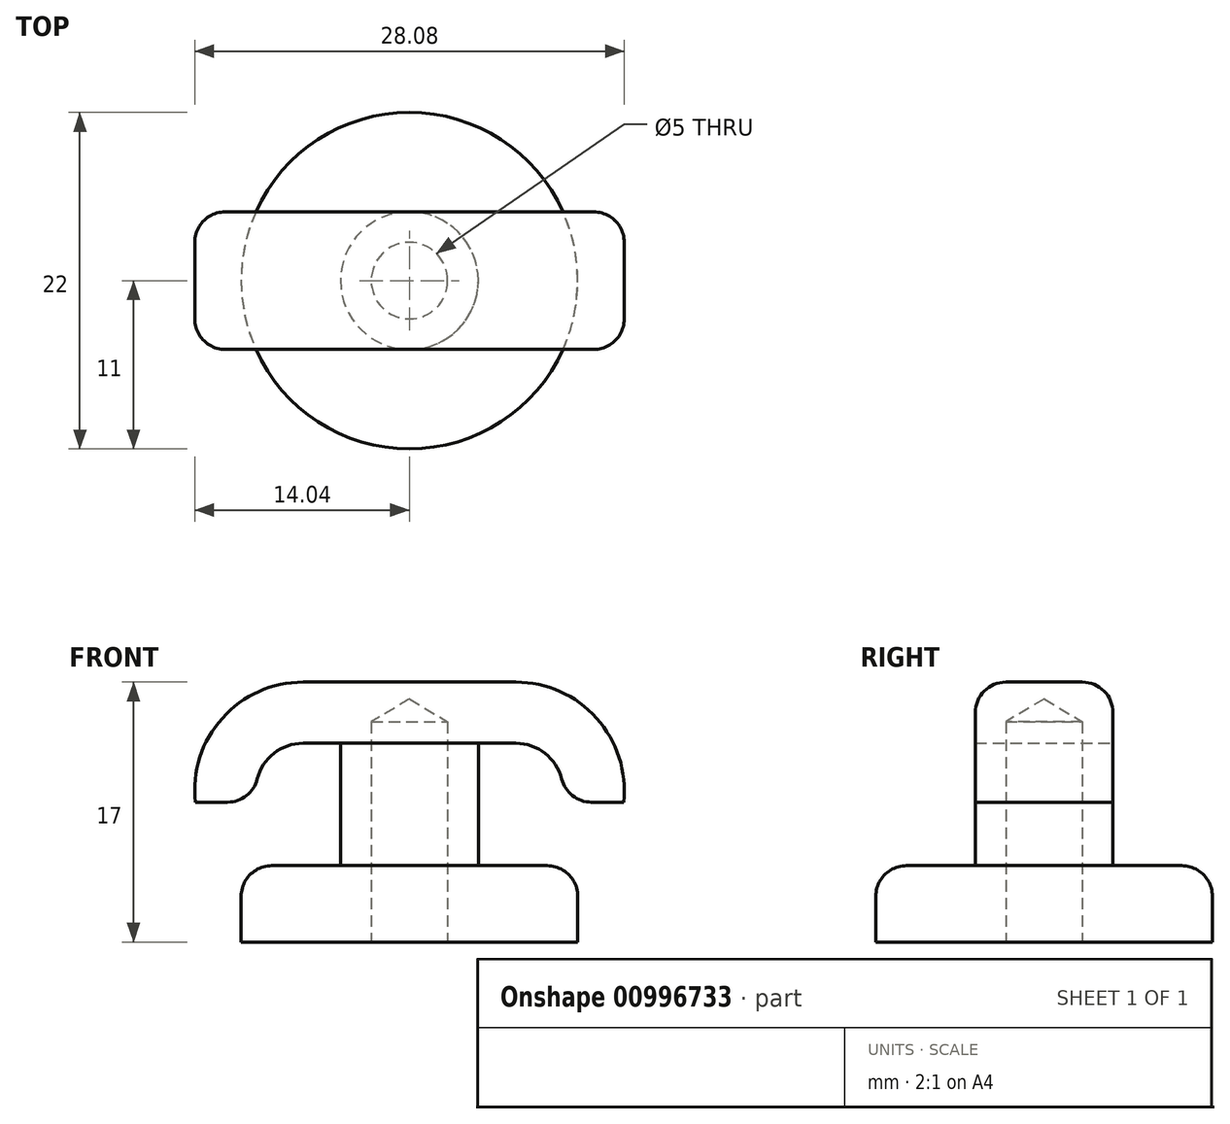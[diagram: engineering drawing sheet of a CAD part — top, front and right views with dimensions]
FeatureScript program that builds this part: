
annotation { "Feature Type Name" : "Feature", "Feature Type Description" : "" }
export const myFeature = defineFeature(function(context is Context, id is Id, definition is map)
    precondition{}
    {
        {
            var Q0;
            Q0=qCreatedBy(makeId("Top.planeOp"),FACE);
            var sketch = newSketch(context, id + "F0", { "sketchPlane" : qUnion([Q0])});
            skCircle(sketch, "E0", {"center": v(0, 0) * mm, "radius": 11 * mm});
            skSolve(sketch);
        }
        {
            var Q0;
            Q0 = qSketchRegion(id + "F0", true);
            extrude(context, id + "F1", {"entities" : qUnion([Q0]), "depth" : 5 * mm, "offsetDistance" : 25 * mm});
        }
        {
            var Q0;
            Q0=makeQuery(id+"F1.opExtrude","CAP_FACE",FACE,{"disambiguationData":[OSD([sQuery(id+"F0.wireOp",EDGE,"E0")])],"isStart":false});
            var sketch = newSketch(context, id + "F2", { "sketchPlane" : qUnion([Q0])});
            skCircle(sketch, "E1", {"center": v(0, 0) * mm, "radius": 4.5 * mm});
            skSolve(sketch);
        }
        {
            var Q0;
            Q0 = qSketchRegion(id + "F2", true);
            extrude(context, id + "F3", {"entities" : qUnion([Q0]), "operationType" : NewBodyOperationType.ADD, "depth" : 12 * mm, "offsetDistance" : 25 * mm});
        }
        {
            var Q0;
            Q0=qCreatedBy(makeId("Front.planeOp"),FACE);
            var sketch = newSketch(context, id + "F4", { "sketchPlane" : qUnion([Q0])});
            skLineSegment(sketch, "E2", {"start": v(0, 13) * mm, "end": v(6.96, 13) * mm});
            skArc(sketch, "E3", {"start": v(9.94, 9.15) * mm, "mid": v(9.4, 11.8) * mm, "end": v(6.96, 13) * mm});
            skLineSegment(sketch, "E4.0", {"start": v(0, 17) * mm, "end": v(6.96, 17) * mm});
            skArc(sketch, "E4.1", {"start": v(14, 9.15) * mm, "mid": v(12.23, 14.65) * mm, "end": v(6.96, 17) * mm});
            skLineSegment(sketch, "E5", {"start": v(9.94, 9.15) * mm, "end": v(14, 9.15) * mm});
            skArc(sketch, "E6.MirrorCS", {"start": v(-9.94, 9.15) * mm, "mid": v(-9.4, 11.8) * mm, "end": v(-6.96, 13) * mm});
            skArc(sketch, "E7.MirrorCS", {"start": v(-14, 9.15) * mm, "mid": v(-12.23, 14.65) * mm, "end": v(-6.96, 17) * mm});
            skLineSegment(sketch, "E8.MirrorCS", {"start": v(0, 13) * mm, "end": v(-6.96, 13) * mm});
            skLineSegment(sketch, "E9.MirrorCS", {"start": v(-9.94, 9.15) * mm, "end": v(-14, 9.15) * mm});
            skLineSegment(sketch, "E10.MirrorCS", {"start": v(0, 17) * mm, "end": v(-6.96, 17) * mm});
            skSolve(sketch);
        }
        {
            var Q0;
            Q0 = qSketchRegion(id + "F4", true);
            extrude(context, id + "F5", {"entities" : qUnion([Q0]), "operationType" : NewBodyOperationType.ADD, "endBound" : BoundingType.SYMMETRIC, "depth" : 9 * mm, "offsetDistance" : 25 * mm});
        }
        {
            var Q0;
            Q0=makeQuery(id+"F1.opExtrude","CAP_EDGE",EDGE,{"disambiguationData":[OSD([sQuery(id+"F0.wireOp",EDGE,"E0")])],"isStart":false});
            var Q1;
            Q1=makeQuery(id+"F5.opExtrude","CAP_EDGE",EDGE,{"disambiguationData":[OSD([sQuery(id+"F4.wireOp",EDGE,"E4.0"),sQuery(id+"F4.wireOp",EDGE,"E10.MirrorCS")])],"isStart":false});
            var Q2;
            Q2=makeQuery(id+"F5.opExtrude","CAP_EDGE",EDGE,{"disambiguationData":[OSD([sQuery(id+"F4.wireOp",EDGE,"E4.0"),sQuery(id+"F4.wireOp",EDGE,"E10.MirrorCS")])],"isStart":true});
            var Q3;
            Q3=makeQuery(id+"F5.opExtrude","SWEPT_EDGE",EDGE,{"disambiguationData":[OSD([sQuery(id+"F4.wireOp",EDGE,"E6.MirrorCS"),sQuery(id+"F4.wireOp",EDGE,"E9.MirrorCS")])]});
            var Q4;
            Q4=makeQuery(id+"F5.opExtrude","SWEPT_EDGE",EDGE,{"disambiguationData":[OSD([sQuery(id+"F4.wireOp",EDGE,"E3"),sQuery(id+"F4.wireOp",EDGE,"E5")])]});
            fillet(context, id + "F6", {"entities" : qUnion([Q0, Q1, Q2, Q3, Q4]), "radius" : 2 * mm, "tangentPropagation" : true, "allowEdgeOverflow" : false});
        }
        {
            var Q0;
            Q0=makeQuery(id+"F1.opExtrude","CAP_FACE",FACE,{"disambiguationData":[OSD([sQuery(id+"F0.wireOp",EDGE,"E0")])],"isStart":true});
            var sketch = newSketch(context, id + "F7", { "sketchPlane" : qUnion([Q0])});
            skPoint(sketch, "E11", {"position": v(0, 0) * mm});
            skSolve(sketch);
        }
        {
            var Q0;
            Q0=sQuery(id+"F7.wireOp",VERTEX,"E11");
            var Q1;
            Q1=makeQuery(id+"F1.opExtrude","SWEPT_BODY",BODY,{"disambiguationData":[OSD([sQuery(id+"F0.wireOp",EDGE,"E0")])]});
            hole(context, id + "F8", {"style" : HoleStyle.SIMPLE, "endStyle" : HoleEndStyle.BLIND, "holeDiameter" : 5 * mm, "majorDiameter" : 5 * mm, "holeDepth" : 14.4 * mm, "isTappedThrough" : true, "tappedDepth" : 12 * mm, "tapClearance" : 3, "locations" : qUnion([Q0]), "scope" : qUnion([Q1])});
        }
    });
